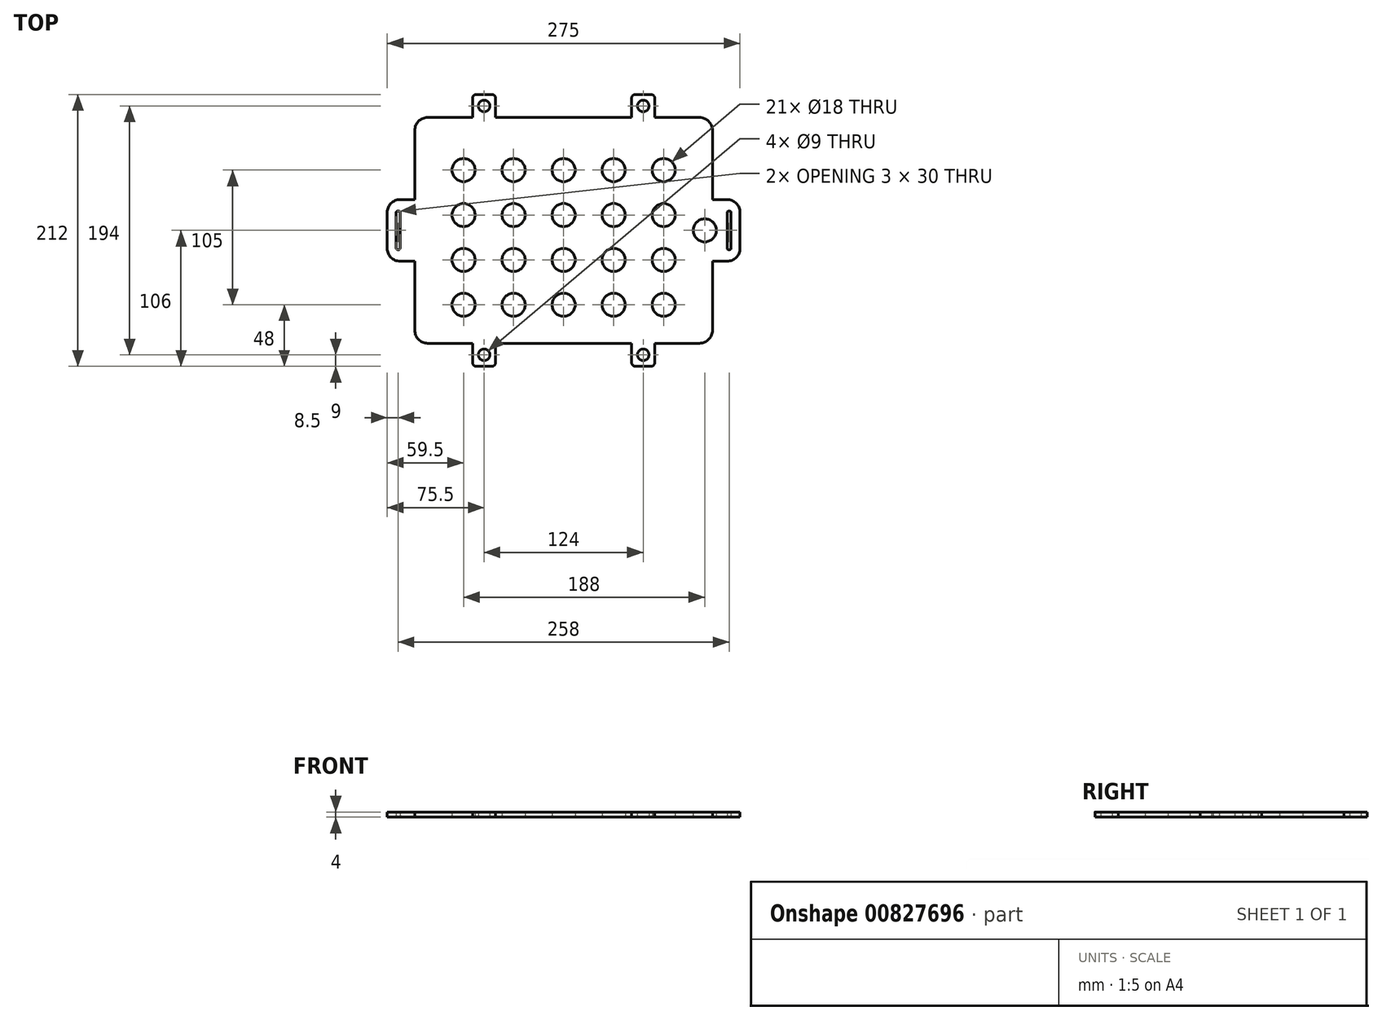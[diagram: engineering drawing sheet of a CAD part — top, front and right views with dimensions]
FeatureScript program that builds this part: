
annotation { "Feature Type Name" : "Feature", "Feature Type Description" : "" }
export const myFeature = defineFeature(function(context is Context, id is Id, definition is map)
    precondition{}
    {
        {
            var Q0;
            Q0=qCreatedBy(makeId("Top.planeOp"),FACE);
            var sketch = newSketch(context, id + "F0", { "sketchPlane" : qUnion([Q0])});
            skLineSegment(sketch, "E0", {"start": v(0, 0) * mm, "end": v(137.5, 0) * mm, "construction": true});
            skLineSegment(sketch, "E1.MirrorCS", {"start": v(0, 0) * mm, "end": v(0, -88) * mm, "construction": true});
            skLineSegment(sketch, "E2.MirrorCS", {"start": v(0, 0) * mm, "end": v(-137.5, 0) * mm, "construction": true});
            skLineSegment(sketch, "E3.bottom", {"start": v(106, -88) * mm, "end": v(71, -88) * mm});
            skLineSegment(sketch, "E3.top", {"start": v(106, 88) * mm, "end": v(71, 88) * mm});
            skLineSegment(sketch, "E3.left", {"start": v(116, -78) * mm, "end": v(116, -24) * mm});
            skLineSegment(sketch, "E3.right", {"start": v(-116, -78) * mm, "end": v(-116, -24) * mm});
            skPoint(sketch, "E3.middle", {"position": v(0, 0) * mm});
            skLineSegment(sketch, "E4", {"start": v(68, 106) * mm, "end": v(56, 106) * mm});
            skPoint(sketch, "E5.orphan", {"position": v(53, 88) * mm});
            skLineSegment(sketch, "E6", {"start": v(71, 103) * mm, "end": v(71, 88) * mm});
            skLineSegment(sketch, "E7.trimOffspring", {"start": v(53, 88) * mm, "end": v(-53, 88) * mm});
            skLineSegment(sketch, "E8.MirrorCS", {"start": v(68, -106) * mm, "end": v(56, -106) * mm});
            skLineSegment(sketch, "E9.MirrorCS", {"start": v(71, -103) * mm, "end": v(71, -88) * mm});
            skLineSegment(sketch, "E10.trimOffspring", {"start": v(53, -88) * mm, "end": v(-53, -88) * mm});
            skLineSegment(sketch, "E11.MirrorCS", {"start": v(-68, -106) * mm, "end": v(-56, -106) * mm});
            skLineSegment(sketch, "E12.MirrorCS", {"start": v(-71, -103) * mm, "end": v(-71, -88) * mm});
            skLineSegment(sketch, "E13.MirrorCS", {"start": v(-68, 106) * mm, "end": v(-56, 106) * mm});
            skLineSegment(sketch, "E14.MirrorCS", {"start": v(-71, 103) * mm, "end": v(-71, 88) * mm});
            skLineSegment(sketch, "E15", {"start": v(-53, -103) * mm, "end": v(-53, -88) * mm});
            skLineSegment(sketch, "E16.trimOffspring", {"start": v(-71, -88) * mm, "end": v(-106, -88) * mm});
            skLineSegment(sketch, "E17", {"start": v(-53, 103) * mm, "end": v(-53, 88) * mm});
            skLineSegment(sketch, "E18.trimOffspring", {"start": v(-71, 88) * mm, "end": v(-106, 88) * mm});
            skLineSegment(sketch, "E19", {"start": v(53, 103) * mm, "end": v(53, 88) * mm});
            skLineSegment(sketch, "E20", {"start": v(53, -103) * mm, "end": v(53, -88) * mm});
            skPoint(sketch, "E21.visualSharp", {"position": v(-71, 106) * mm});
            skArc(sketch, "E21.filletArc", {"start": v(-68, 106) * mm, "mid": v(-70.12, 105.12) * mm, "end": v(-71, 103) * mm});
            skPoint(sketch, "E22.visualSharp", {"position": v(-53, 106) * mm});
            skArc(sketch, "E22.filletArc", {"start": v(-53, 103) * mm, "mid": v(-53.88, 105.12) * mm, "end": v(-56, 106) * mm});
            skPoint(sketch, "E23.visualSharp", {"position": v(53, 106) * mm});
            skArc(sketch, "E23.filletArc", {"start": v(56, 106) * mm, "mid": v(53.88, 105.12) * mm, "end": v(53, 103) * mm});
            skPoint(sketch, "E24.visualSharp", {"position": v(71, 106) * mm});
            skArc(sketch, "E24.filletArc", {"start": v(71, 103) * mm, "mid": v(70.12, 105.12) * mm, "end": v(68, 106) * mm});
            skPoint(sketch, "E25.visualSharp", {"position": v(-71, -106) * mm});
            skArc(sketch, "E25.filletArc", {"start": v(-71, -103) * mm, "mid": v(-70.12, -105.12) * mm, "end": v(-68, -106) * mm});
            skPoint(sketch, "E26.visualSharp", {"position": v(-53, -106) * mm});
            skArc(sketch, "E26.filletArc", {"start": v(-56, -106) * mm, "mid": v(-53.88, -105.12) * mm, "end": v(-53, -103) * mm});
            skPoint(sketch, "E27.visualSharp", {"position": v(53, -106) * mm});
            skArc(sketch, "E27.filletArc", {"start": v(53, -103) * mm, "mid": v(53.88, -105.12) * mm, "end": v(56, -106) * mm});
            skPoint(sketch, "E28.visualSharp", {"position": v(71, -106) * mm});
            skArc(sketch, "E28.filletArc", {"start": v(68, -106) * mm, "mid": v(70.12, -105.12) * mm, "end": v(71, -103) * mm});
            skLineSegment(sketch, "E29", {"start": v(137.5, -14) * mm, "end": v(137.5, 14) * mm});
            skLineSegment(sketch, "E30", {"start": v(127.5, 24) * mm, "end": v(116, 24) * mm});
            skLineSegment(sketch, "E31.MirrorCS", {"start": v(127.5, -24) * mm, "end": v(116, -24) * mm});
            skPoint(sketch, "E32.orphan", {"position": v(137.5, 53.3) * mm});
            skLineSegment(sketch, "E33.trimOffspring", {"start": v(116, 24) * mm, "end": v(116, 78) * mm});
            skPoint(sketch, "E34.orphan", {"position": v(0, 24) * mm});
            skPoint(sketch, "E35.orphan", {"position": v(0, -24) * mm});
            skPoint(sketch, "E36.visualSharp", {"position": v(137.5, 24) * mm});
            skArc(sketch, "E36.filletArc", {"start": v(137.5, 14) * mm, "mid": v(134.57, 21.07) * mm, "end": v(127.5, 24) * mm});
            skPoint(sketch, "E37.visualSharp", {"position": v(137.5, -24) * mm});
            skArc(sketch, "E37.filletArc", {"start": v(127.5, -24) * mm, "mid": v(134.57, -21.07) * mm, "end": v(137.5, -14) * mm});
            skLineSegment(sketch, "E38", {"start": v(127.5, 15) * mm, "end": v(130.5, 15) * mm});
            skPoint(sketch, "E39.trimOffspring.end.orphan", {"position": v(146.66, 15) * mm});
            skLineSegment(sketch, "E40.MirrorCS", {"start": v(127.5, -15) * mm, "end": v(130.5, -15) * mm});
            skLineSegment(sketch, "E41.MirrorCS", {"start": v(-127.5, 24) * mm, "end": v(-116, 24) * mm});
            skArc(sketch, "E42.MirrorCS", {"start": v(-137.5, 14) * mm, "mid": v(-134.57, 21.07) * mm, "end": v(-127.5, 24) * mm});
            skLineSegment(sketch, "E43.MirrorCS", {"start": v(-137.5, -14) * mm, "end": v(-137.5, 14) * mm});
            skArc(sketch, "E44.MirrorCS", {"start": v(-127.5, -24) * mm, "mid": v(-134.57, -21.07) * mm, "end": v(-137.5, -14) * mm});
            skLineSegment(sketch, "E45.MirrorCS", {"start": v(-127.5, -24) * mm, "end": v(-116, -24) * mm});
            skLineSegment(sketch, "E46.MirrorCS", {"start": v(-127.5, 0) * mm, "end": v(-127.5, 15) * mm});
            skLineSegment(sketch, "E47.MirrorCS", {"start": v(-130.5, 0) * mm, "end": v(-130.5, 15) * mm});
            skLineSegment(sketch, "E48.MirrorCS", {"start": v(-130.5, 0) * mm, "end": v(-130.5, -15) * mm});
            skLineSegment(sketch, "E49.MirrorCS", {"start": v(-127.5, 0) * mm, "end": v(-127.5, -15) * mm});
            skLineSegment(sketch, "E50.MirrorCS", {"start": v(-127.5, 15) * mm, "end": v(-130.5, 15) * mm});
            skLineSegment(sketch, "E51.MirrorCS", {"start": v(-127.5, -15) * mm, "end": v(-130.5, -15) * mm});
            skLineSegment(sketch, "E52.trimOffspring", {"start": v(-116, 24) * mm, "end": v(-116, 78) * mm});
            skPoint(sketch, "E53.visualSharp", {"position": v(-116, 88) * mm});
            skArc(sketch, "E53.filletArc", {"start": v(-106, 88) * mm, "mid": v(-113.07, 85.07) * mm, "end": v(-116, 78) * mm});
            skPoint(sketch, "E54.visualSharp", {"position": v(-116, -88) * mm});
            skArc(sketch, "E54.filletArc", {"start": v(-116, -78) * mm, "mid": v(-113.07, -85.07) * mm, "end": v(-106, -88) * mm});
            skPoint(sketch, "E55.visualSharp", {"position": v(116, -88) * mm});
            skArc(sketch, "E55.filletArc", {"start": v(106, -88) * mm, "mid": v(113.07, -85.07) * mm, "end": v(116, -78) * mm});
            skPoint(sketch, "E56.visualSharp", {"position": v(116, 88) * mm});
            skArc(sketch, "E56.filletArc", {"start": v(116, 78) * mm, "mid": v(113.07, 85.07) * mm, "end": v(106, 88) * mm});
            skLineSegment(sketch, "E57", {"start": v(127.5, -15) * mm, "end": v(127.5, 15) * mm});
            skLineSegment(sketch, "E58", {"start": v(130.5, -15) * mm, "end": v(130.5, 15) * mm});
            skLineSegment(sketch, "E59.MirrorCS", {"start": v(78, 0) * mm, "end": v(78, 88) * mm, "construction": true});
            skPoint(sketch, "E60.MirrorP", {"position": v(78, -24) * mm});
            skLineSegment(sketch, "E61.MirrorCS", {"start": v(78, 0) * mm, "end": v(78, -88) * mm, "construction": true});
            skLineSegment(sketch, "E62.MirrorCS", {"start": v(-78, 0) * mm, "end": v(-78, 88) * mm, "construction": true});
            skLineSegment(sketch, "E63.MirrorCS", {"start": v(-78, 0) * mm, "end": v(-78, -88) * mm, "construction": true});
            skCircle(sketch, "E64", {"center": v(-78, -23) * mm, "radius": 9 * mm});
            skCircle(sketch, "E65.MirrorC", {"center": v(-78, 47) * mm, "radius": 9 * mm});
            skCircle(sketch, "E66", {"center": v(-78, -58) * mm, "radius": 9 * mm});
            skCircle(sketch, "E67.MirrorC", {"center": v(-78, 12) * mm, "radius": 9 * mm});
            skCircle(sketch, "E68.MirrorC", {"center": v(0, 47) * mm, "radius": 9 * mm});
            skCircle(sketch, "E69.MirrorC", {"center": v(0, 12) * mm, "radius": 9 * mm});
            skCircle(sketch, "E70.MirrorC", {"center": v(0, -23) * mm, "radius": 9 * mm});
            skCircle(sketch, "E71.MirrorC", {"center": v(0, -58) * mm, "radius": 9 * mm});
            skCircle(sketch, "E72.MirrorC", {"center": v(78, 47) * mm, "radius": 9 * mm});
            skCircle(sketch, "E73.MirrorC", {"center": v(78, 12) * mm, "radius": 9 * mm});
            skCircle(sketch, "E74.MirrorC", {"center": v(78, -23) * mm, "radius": 9 * mm});
            skCircle(sketch, "E75.MirrorC", {"center": v(78, -58) * mm, "radius": 9 * mm});
            skCircle(sketch, "E76.1.0.0", {"center": v(39, 47) * mm, "radius": 9 * mm});
            skCircle(sketch, "E76.1.0.1", {"center": v(39, 12) * mm, "radius": 9 * mm});
            skCircle(sketch, "E76.1.0.2", {"center": v(39, -23) * mm, "radius": 9 * mm});
            skCircle(sketch, "E76.1.0.3", {"center": v(39, -58) * mm, "radius": 9 * mm});
            skCircle(sketch, "E77.MirrorC", {"center": v(-39, 47) * mm, "radius": 9 * mm});
            skCircle(sketch, "E78.MirrorC", {"center": v(-39, 12) * mm, "radius": 9 * mm});
            skCircle(sketch, "E79.MirrorC", {"center": v(-39, -23) * mm, "radius": 9 * mm});
            skCircle(sketch, "E80.MirrorC", {"center": v(-39, -58) * mm, "radius": 9 * mm});
            skPoint(sketch, "E81.orphan", {"position": v(-77.85, 97) * mm});
            skCircle(sketch, "E82", {"center": v(-62, 97) * mm, "radius": 4.5 * mm});
            skCircle(sketch, "E83.MirrorC", {"center": v(62, 97) * mm, "radius": 4.5 * mm});
            skCircle(sketch, "E84.MirrorC", {"center": v(-62, -97) * mm, "radius": 4.5 * mm});
            skCircle(sketch, "E85.MirrorC", {"center": v(62, -97) * mm, "radius": 4.5 * mm});
            skLineSegment(sketch, "E86", {"start": v(110, -88) * mm, "end": v(110, 88) * mm, "construction": true});
            skCircle(sketch, "E87", {"center": v(110, 0) * mm, "radius": 9 * mm});
            skSolve(sketch);
        }
        {
            var Q0;
            Q0=qSketchRegion(id+"F0",true);
            extrude(context, id + "F1", {"entities" : qUnion([Q0]), "depth" : 4 * mm, "offsetDistance" : 25 * mm});
        }
        {
            var Q0;
            Q0=makeQuery(id+"F1.opExtrude","SWEPT_EDGE",EDGE,{"disambiguationData":[OSD([sQuery(id+"F0.wireOp",EDGE,"E40.MirrorCS"),sQuery(id+"F0.wireOp",EDGE,"E57")])]});
            var Q1;
            Q1=makeQuery(id+"F1.opExtrude","SWEPT_EDGE",EDGE,{"disambiguationData":[OSD([sQuery(id+"F0.wireOp",EDGE,"E40.MirrorCS"),sQuery(id+"F0.wireOp",EDGE,"E58")])]});
            fillet(context, id + "F2", {"entities" : qUnion([Q0, Q1]), "radius" : 1 * mm, "tangentPropagation" : true, "allowEdgeOverflow" : false});
        }
        {
            var Q0;
            Q0=makeQuery(id+"F1.opExtrude","SWEPT_EDGE",EDGE,{"disambiguationData":[OSD([sQuery(id+"F0.wireOp",EDGE,"E38"),sQuery(id+"F0.wireOp",EDGE,"E57")])]});
            var Q1;
            Q1=makeQuery(id+"F1.opExtrude","SWEPT_EDGE",EDGE,{"disambiguationData":[OSD([sQuery(id+"F0.wireOp",EDGE,"E38"),sQuery(id+"F0.wireOp",EDGE,"E58")])]});
            fillet(context, id + "F3", {"entities" : qUnion([Q0, Q1]), "radius" : 1 * mm, "tangentPropagation" : true, "allowEdgeOverflow" : false});
        }
        {
            var Q0;
            Q0=makeQuery(id+"F1.opExtrude","SWEPT_EDGE",EDGE,{"disambiguationData":[OSD([sQuery(id+"F0.wireOp",EDGE,"E47.MirrorCS"),sQuery(id+"F0.wireOp",EDGE,"E50.MirrorCS")])]});
            var Q1;
            Q1=makeQuery(id+"F1.opExtrude","SWEPT_EDGE",EDGE,{"disambiguationData":[OSD([sQuery(id+"F0.wireOp",EDGE,"E46.MirrorCS"),sQuery(id+"F0.wireOp",EDGE,"E50.MirrorCS")])]});
            fillet(context, id + "F4", {"entities" : qUnion([Q0, Q1]), "radius" : 1 * mm, "tangentPropagation" : true, "allowEdgeOverflow" : false});
        }
        {
            var Q0;
            Q0=makeQuery(id+"F1.opExtrude","SWEPT_EDGE",EDGE,{"disambiguationData":[OSD([sQuery(id+"F0.wireOp",EDGE,"E48.MirrorCS"),sQuery(id+"F0.wireOp",EDGE,"E51.MirrorCS")])]});
            var Q1;
            Q1=makeQuery(id+"F1.opExtrude","SWEPT_EDGE",EDGE,{"disambiguationData":[OSD([sQuery(id+"F0.wireOp",EDGE,"E49.MirrorCS"),sQuery(id+"F0.wireOp",EDGE,"E51.MirrorCS")])]});
            fillet(context, id + "F5", {"entities" : qUnion([Q0, Q1]), "radius" : 1 * mm, "tangentPropagation" : true, "allowEdgeOverflow" : false});
        }
    });
